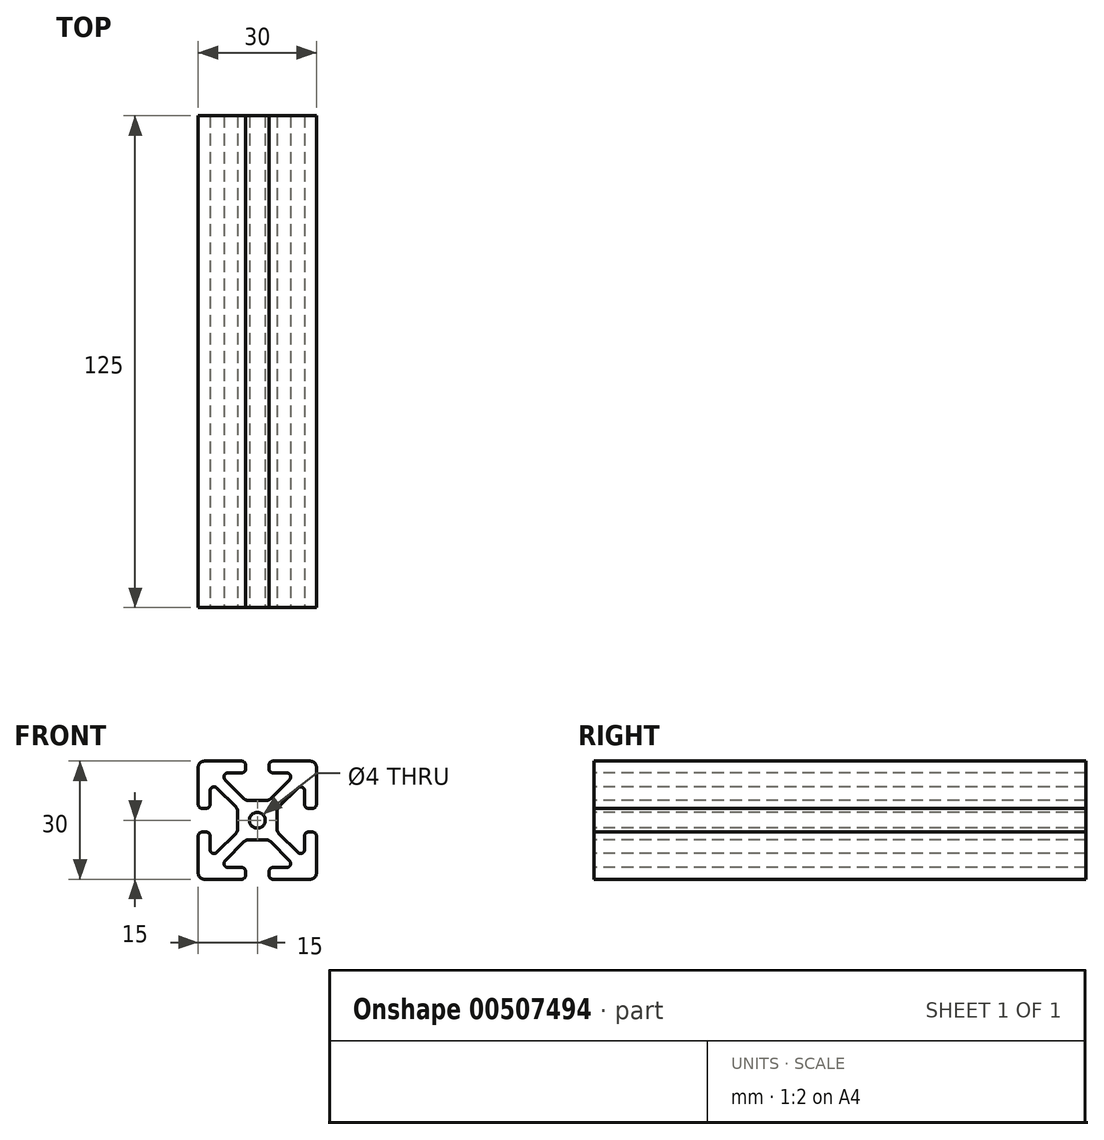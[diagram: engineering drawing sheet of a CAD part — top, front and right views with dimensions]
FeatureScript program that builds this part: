
annotation { "Feature Type Name" : "Feature", "Feature Type Description" : "" }
export const myFeature = defineFeature(function(context is Context, id is Id, definition is map)
    precondition{}
    {
        {
            var Q0;
            Q0=qCreatedBy(makeId("Front.planeOp"),FACE);
            var sketch = newSketch(context, id + "F0", { "sketchPlane" : qUnion([Q0])});
            skLineSegment(sketch, "E0.bottom", {"start": v(13.5, 15) * mm, "end": v(4, 15) * mm});
            skLineSegment(sketch, "E0.top", {"start": v(13.5, -15) * mm, "end": v(4, -15) * mm});
            skLineSegment(sketch, "E0.left", {"start": v(15, 13.5) * mm, "end": v(15, 4) * mm});
            skLineSegment(sketch, "E0.right", {"start": v(-15, 13.5) * mm, "end": v(-15, 4) * mm});
            skPoint(sketch, "E0.middle", {"position": v(0, 0) * mm});
            skLineSegment(sketch, "E1.bottom", {"start": v(7.46, 12) * mm, "end": v(4, 12) * mm});
            skLineSegment(sketch, "E1.top", {"start": v(7.46, -12) * mm, "end": v(4, -12) * mm});
            skLineSegment(sketch, "E1.left", {"start": v(12, 7.46) * mm, "end": v(12, 4) * mm});
            skLineSegment(sketch, "E1.right", {"start": v(-12, 7.46) * mm, "end": v(-12, 4) * mm});
            skLineSegment(sketch, "E2", {"start": v(8.17, 10.3) * mm, "end": v(3.32, 5.44) * mm});
            skLineSegment(sketch, "E3", {"start": v(-8.17, -10.3) * mm, "end": v(-3.32, -5.44) * mm});
            skLineSegment(sketch, "E4", {"start": v(-8.17, 10.3) * mm, "end": v(-3.32, 5.44) * mm});
            skLineSegment(sketch, "E5", {"start": v(-10.3, 8.17) * mm, "end": v(-5.44, 3.32) * mm});
            skPoint(sketch, "E6.orphan", {"position": v(12, 12) * mm});
            skPoint(sketch, "E7.orphan", {"position": v(12, -12) * mm});
            skPoint(sketch, "E8.orphan", {"position": v(-12, -12) * mm});
            skPoint(sketch, "E9.orphan", {"position": v(-12, 12) * mm});
            skLineSegment(sketch, "E10.trimOffspring", {"start": v(-5.44, -3.32) * mm, "end": v(-10.3, -8.17) * mm});
            skLineSegment(sketch, "E11.trimOffspring", {"start": v(5.44, -3.32) * mm, "end": v(10.3, -8.17) * mm});
            skLineSegment(sketch, "E12.trimOffspring", {"start": v(5.44, 3.32) * mm, "end": v(10.3, 8.17) * mm});
            skLineSegment(sketch, "E13.trimOffspring", {"start": v(3.32, -5.44) * mm, "end": v(8.17, -10.3) * mm});
            skLineSegment(sketch, "E14.bottom", {"start": v(2.26, 5) * mm, "end": v(-2.26, 5) * mm});
            skLineSegment(sketch, "E14.top", {"start": v(2.26, -5) * mm, "end": v(-2.26, -5) * mm});
            skLineSegment(sketch, "E14.left", {"start": v(5, 2.26) * mm, "end": v(5, -2.26) * mm});
            skLineSegment(sketch, "E14.right", {"start": v(-5, 2.26) * mm, "end": v(-5, -2.26) * mm});
            skPoint(sketch, "E15.orphan", {"position": v(5, 5) * mm});
            skPoint(sketch, "E16.orphan", {"position": v(5, -5) * mm});
            skPoint(sketch, "E17.orphan", {"position": v(-5, -5) * mm});
            skPoint(sketch, "E18.orphan", {"position": v(-5, 5) * mm});
            skCircle(sketch, "E19", {"center": v(0, 0) * mm, "radius": 2 * mm});
            skLineSegment(sketch, "E20", {"start": v(-3, 14) * mm, "end": v(-3, 13) * mm});
            skLineSegment(sketch, "E21", {"start": v(3, 14) * mm, "end": v(3, 13) * mm});
            skLineSegment(sketch, "E22.trimOffspring", {"start": v(-3, -13) * mm, "end": v(-3, -14) * mm});
            skLineSegment(sketch, "E23.trimOffspring", {"start": v(-4, 12) * mm, "end": v(-7.46, 12) * mm});
            skLineSegment(sketch, "E24.trimOffspring", {"start": v(-4, 15) * mm, "end": v(-13.5, 15) * mm});
            skLineSegment(sketch, "E25.trimOffspring", {"start": v(3, -13) * mm, "end": v(3, -14) * mm});
            skLineSegment(sketch, "E26.trimOffspring", {"start": v(-4, -12) * mm, "end": v(-7.46, -12) * mm});
            skLineSegment(sketch, "E27.trimOffspring", {"start": v(-4, -15) * mm, "end": v(-13.5, -15) * mm});
            skLineSegment(sketch, "E28", {"start": v(-14, 3) * mm, "end": v(-13, 3) * mm});
            skLineSegment(sketch, "E29", {"start": v(-14, -3) * mm, "end": v(-13, -3) * mm});
            skLineSegment(sketch, "E30.trimOffspring", {"start": v(-12, -4) * mm, "end": v(-12, -7.46) * mm});
            skLineSegment(sketch, "E31.trimOffspring", {"start": v(-15, -4) * mm, "end": v(-15, -13.5) * mm});
            skLineSegment(sketch, "E32.trimOffspring", {"start": v(13, 3) * mm, "end": v(14, 3) * mm});
            skLineSegment(sketch, "E33.trimOffspring", {"start": v(13, -3) * mm, "end": v(14, -3) * mm});
            skLineSegment(sketch, "E34.trimOffspring", {"start": v(12, -4) * mm, "end": v(12, -7.46) * mm});
            skLineSegment(sketch, "E35.trimOffspring", {"start": v(15, -4) * mm, "end": v(15, -13.5) * mm});
            skPoint(sketch, "E36.visualSharp", {"position": v(-15, 15) * mm});
            skArc(sketch, "E36.filletArc", {"start": v(-13.5, 15) * mm, "mid": v(-14.56, 14.56) * mm, "end": v(-15, 13.5) * mm});
            skPoint(sketch, "E37.visualSharp", {"position": v(15, 15) * mm});
            skArc(sketch, "E37.filletArc", {"start": v(15, 13.5) * mm, "mid": v(14.56, 14.56) * mm, "end": v(13.5, 15) * mm});
            skPoint(sketch, "E38.visualSharp", {"position": v(15, -15) * mm});
            skArc(sketch, "E38.filletArc", {"start": v(13.5, -15) * mm, "mid": v(14.56, -14.56) * mm, "end": v(15, -13.5) * mm});
            skPoint(sketch, "E39.visualSharp", {"position": v(-15, -15) * mm});
            skArc(sketch, "E39.filletArc", {"start": v(-15, -13.5) * mm, "mid": v(-14.56, -14.56) * mm, "end": v(-13.5, -15) * mm});
            skPoint(sketch, "E40.visualSharp", {"position": v(-5, -2.88) * mm});
            skArc(sketch, "E40.filletArc", {"start": v(-5.44, -3.32) * mm, "mid": v(-5.11, -2.83) * mm, "end": v(-5, -2.26) * mm});
            skPoint(sketch, "E41.visualSharp", {"position": v(-2.88, -5) * mm});
            skArc(sketch, "E41.filletArc", {"start": v(-2.26, -5) * mm, "mid": v(-2.83, -5.11) * mm, "end": v(-3.32, -5.44) * mm});
            skPoint(sketch, "E42.visualSharp", {"position": v(2.88, -5) * mm});
            skArc(sketch, "E42.filletArc", {"start": v(3.32, -5.44) * mm, "mid": v(2.83, -5.11) * mm, "end": v(2.26, -5) * mm});
            skPoint(sketch, "E43.visualSharp", {"position": v(5, -2.88) * mm});
            skArc(sketch, "E43.filletArc", {"start": v(5, -2.26) * mm, "mid": v(5.11, -2.83) * mm, "end": v(5.44, -3.32) * mm});
            skPoint(sketch, "E44.visualSharp", {"position": v(5, 2.88) * mm});
            skArc(sketch, "E44.filletArc", {"start": v(5.44, 3.32) * mm, "mid": v(5.11, 2.83) * mm, "end": v(5, 2.26) * mm});
            skPoint(sketch, "E45.visualSharp", {"position": v(2.88, 5) * mm});
            skArc(sketch, "E45.filletArc", {"start": v(2.26, 5) * mm, "mid": v(2.83, 5.11) * mm, "end": v(3.32, 5.44) * mm});
            skPoint(sketch, "E46.visualSharp", {"position": v(-2.88, 5) * mm});
            skArc(sketch, "E46.filletArc", {"start": v(-3.32, 5.44) * mm, "mid": v(-2.83, 5.11) * mm, "end": v(-2.26, 5) * mm});
            skPoint(sketch, "E47.visualSharp", {"position": v(-3, 12) * mm});
            skArc(sketch, "E47.filletArc", {"start": v(-4, 12) * mm, "mid": v(-3.3, 12.3) * mm, "end": v(-3, 13) * mm});
            skPoint(sketch, "E48.visualSharp", {"position": v(-3, 15) * mm});
            skArc(sketch, "E48.filletArc", {"start": v(-3, 14) * mm, "mid": v(-3.3, 14.7) * mm, "end": v(-4, 15) * mm});
            skPoint(sketch, "E49.visualSharp", {"position": v(3, 15) * mm});
            skArc(sketch, "E49.filletArc", {"start": v(4, 15) * mm, "mid": v(3.3, 14.7) * mm, "end": v(3, 14) * mm});
            skPoint(sketch, "E50.visualSharp", {"position": v(3, 12) * mm});
            skArc(sketch, "E50.filletArc", {"start": v(3, 13) * mm, "mid": v(3.3, 12.3) * mm, "end": v(4, 12) * mm});
            skPoint(sketch, "E51.visualSharp", {"position": v(12, 3) * mm});
            skArc(sketch, "E51.filletArc", {"start": v(12, 4) * mm, "mid": v(12.3, 3.3) * mm, "end": v(13, 3) * mm});
            skPoint(sketch, "E52.visualSharp", {"position": v(15, 3) * mm});
            skArc(sketch, "E52.filletArc", {"start": v(14, 3) * mm, "mid": v(14.7, 3.3) * mm, "end": v(15, 4) * mm});
            skPoint(sketch, "E53.visualSharp", {"position": v(15, -3) * mm});
            skArc(sketch, "E53.filletArc", {"start": v(15, -4) * mm, "mid": v(14.7, -3.3) * mm, "end": v(14, -3) * mm});
            skPoint(sketch, "E54.visualSharp", {"position": v(12, -3) * mm});
            skArc(sketch, "E54.filletArc", {"start": v(13, -3) * mm, "mid": v(12.3, -3.3) * mm, "end": v(12, -4) * mm});
            skPoint(sketch, "E55.visualSharp", {"position": v(3, -12) * mm});
            skArc(sketch, "E55.filletArc", {"start": v(4, -12) * mm, "mid": v(3.3, -12.3) * mm, "end": v(3, -13) * mm});
            skPoint(sketch, "E56.visualSharp", {"position": v(3, -15) * mm});
            skArc(sketch, "E56.filletArc", {"start": v(3, -14) * mm, "mid": v(3.3, -14.7) * mm, "end": v(4, -15) * mm});
            skPoint(sketch, "E57.visualSharp", {"position": v(-3, -12) * mm});
            skArc(sketch, "E57.filletArc", {"start": v(-3, -13) * mm, "mid": v(-3.3, -12.3) * mm, "end": v(-4, -12) * mm});
            skPoint(sketch, "E58.visualSharp", {"position": v(-3, -15) * mm});
            skArc(sketch, "E58.filletArc", {"start": v(-4, -15) * mm, "mid": v(-3.3, -14.7) * mm, "end": v(-3, -14) * mm});
            skPoint(sketch, "E59.visualSharp", {"position": v(-12, -3) * mm});
            skArc(sketch, "E59.filletArc", {"start": v(-12, -4) * mm, "mid": v(-12.3, -3.3) * mm, "end": v(-13, -3) * mm});
            skPoint(sketch, "E60.visualSharp", {"position": v(-15, -3) * mm});
            skArc(sketch, "E60.filletArc", {"start": v(-14, -3) * mm, "mid": v(-14.7, -3.3) * mm, "end": v(-15, -4) * mm});
            skPoint(sketch, "E61.visualSharp", {"position": v(-15, 3) * mm});
            skArc(sketch, "E61.filletArc", {"start": v(-15, 4) * mm, "mid": v(-14.7, 3.3) * mm, "end": v(-14, 3) * mm});
            skPoint(sketch, "E62.visualSharp", {"position": v(-12, 3) * mm});
            skArc(sketch, "E62.filletArc", {"start": v(-13, 3) * mm, "mid": v(-12.3, 3.3) * mm, "end": v(-12, 4) * mm});
            skPoint(sketch, "E63.visualSharp", {"position": v(9.88, 12) * mm});
            skArc(sketch, "E63.filletArc", {"start": v(8.17, 10.3) * mm, "mid": v(8.39, 11.38) * mm, "end": v(7.46, 12) * mm});
            skPoint(sketch, "E64.visualSharp", {"position": v(12, 9.88) * mm});
            skArc(sketch, "E64.filletArc", {"start": v(12, 7.46) * mm, "mid": v(11.38, 8.39) * mm, "end": v(10.3, 8.17) * mm});
            skPoint(sketch, "E65.visualSharp", {"position": v(12, -9.88) * mm});
            skArc(sketch, "E65.filletArc", {"start": v(10.3, -8.17) * mm, "mid": v(11.38, -8.39) * mm, "end": v(12, -7.46) * mm});
            skPoint(sketch, "E66.visualSharp", {"position": v(9.88, -12) * mm});
            skArc(sketch, "E66.filletArc", {"start": v(7.46, -12) * mm, "mid": v(8.39, -11.38) * mm, "end": v(8.17, -10.3) * mm});
            skPoint(sketch, "E67.visualSharp", {"position": v(-12, -9.88) * mm});
            skArc(sketch, "E67.filletArc", {"start": v(-12, -7.46) * mm, "mid": v(-11.38, -8.39) * mm, "end": v(-10.3, -8.17) * mm});
            skPoint(sketch, "E68.visualSharp", {"position": v(-9.88, -12) * mm});
            skArc(sketch, "E68.filletArc", {"start": v(-8.17, -10.3) * mm, "mid": v(-8.39, -11.38) * mm, "end": v(-7.46, -12) * mm});
            skPoint(sketch, "E69.visualSharp", {"position": v(-12, 9.88) * mm});
            skArc(sketch, "E69.filletArc", {"start": v(-10.3, 8.17) * mm, "mid": v(-11.38, 8.39) * mm, "end": v(-12, 7.46) * mm});
            skPoint(sketch, "E70.visualSharp", {"position": v(-9.88, 12) * mm});
            skArc(sketch, "E70.filletArc", {"start": v(-7.46, 12) * mm, "mid": v(-8.39, 11.38) * mm, "end": v(-8.17, 10.3) * mm});
            skPoint(sketch, "E71.visualSharp", {"position": v(-5, 2.88) * mm});
            skArc(sketch, "E71.filletArc", {"start": v(-5, 2.26) * mm, "mid": v(-5.11, 2.83) * mm, "end": v(-5.44, 3.32) * mm});
            skSolve(sketch);
        }
        {
            var Q0;
            Q0=qSketchRegion(id+"F0",true);
            extrude(context, id + "F1", {"entities" : qUnion([Q0]), "oppositeDirection" : true, "depth" : 125 * mm});
        }
    });
